# Revit family: Curtainwall_T2000-Series-Door-Opening_Cross-Aluminum
name_source: partatom
category: Generic Models
units: mm (PartAtom-declared; Revit-internal decimal feet)

## family parameters
Always vertical = Yes
Can host rebar = No
Cut with Voids When Loaded = No
Host = Wall
Maintain Annotation Orientation = No
Part Type = Normal
Room Calculation Point = No
Round Connector Dimension = Use Diameter
Shared = No

## types (1)
- T2000-Series-Door-Opening
    Default Elevation = 0' - 0"
    Door Height = 7' - 0 7/8"
    Door Width = 6' - 5 1/2"
    Frame Depth (4-1/4” to 9-1/4”) = 0' - 6 1/2"
    Frame Depth (4-1/4” to 9-1/4”) Limit = 0' - 6 1/2"
    Frame Material = Frame
    Keynote = 08 44 00
    Manufacturer = Cross Aluminum
    Model = T2000-Series-Door-Opening
    Product Page URL = https://www.crossaluminum.com
    Rough Height = 7' - 3 1/4"
    Rough Width = 6' - 10 1/4"
    URL = https://www.crossaluminum.com

## geometry (parser evidence)
native form markers: Sweep x6
no freeform markers — native parametric forms only
